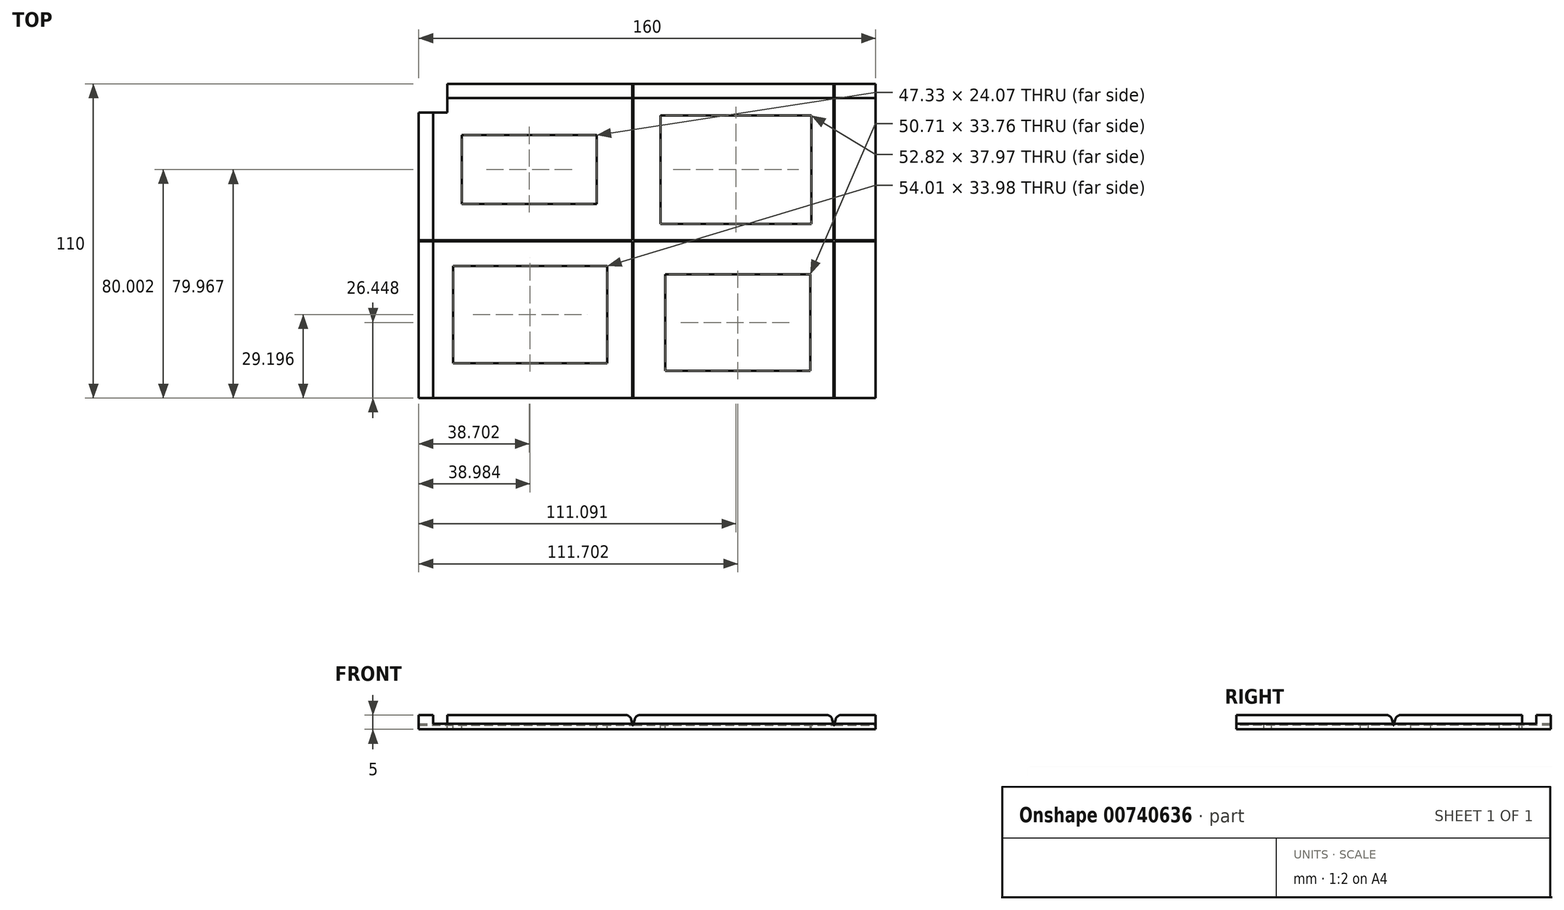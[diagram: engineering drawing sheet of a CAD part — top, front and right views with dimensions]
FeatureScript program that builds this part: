
annotation { "Feature Type Name" : "Feature", "Feature Type Description" : "" }
export const myFeature = defineFeature(function(context is Context, id is Id, definition is map)
    precondition{}
    {
        {
            var Q0;
            Q0=qCreatedBy(makeId("Top.planeOp"),FACE);
            var sketch = newSketch(context, id + "F0", { "sketchPlane" : qUnion([Q0])});
            skLineSegment(sketch, "E0.bottom", {"start": v(-39.4, 71.12) * mm, "end": v(120.6, 71.12) * mm});
            skLineSegment(sketch, "E0.top", {"start": v(-39.4, -38.88) * mm, "end": v(120.6, -38.88) * mm});
            skLineSegment(sketch, "E0.left", {"start": v(-39.4, 71.12) * mm, "end": v(-39.4, -38.88) * mm});
            skLineSegment(sketch, "E0.right", {"start": v(120.6, 71.12) * mm, "end": v(120.6, -38.88) * mm});
            skSolve(sketch);
        }
        {
            var Q0;
            Q0 = qSketchRegion(id + "F0", true);
            extrude(context, id + "F1", {"entities" : qUnion([Q0]), "depth" : 2 * mm, "offsetDistance" : 25 * mm});
        }
        {
            var Q0;
            Q0=makeQuery(id+"F1.opExtrude","CAP_FACE",FACE,{"disambiguationData":[OSD([sQuery(id+"F0.wireOp",EDGE,"E0.bottom"),sQuery(id+"F0.wireOp",EDGE,"E0.top"),sQuery(id+"F0.wireOp",EDGE,"E0.left"),sQuery(id+"F0.wireOp",EDGE,"E0.right")])],"isStart":false});
            var sketch = newSketch(context, id + "F2", { "sketchPlane" : qUnion([Q0])});
            skLineSegment(sketch, "E1.bottom", {"start": v(-39.4, 71.12) * mm, "end": v(-34.4, 71.12) * mm});
            skLineSegment(sketch, "E1.top", {"start": v(-39.4, -38.88) * mm, "end": v(-34.4, -38.88) * mm});
            skLineSegment(sketch, "E1.left", {"start": v(-39.4, 71.12) * mm, "end": v(-39.4, -38.88) * mm});
            skLineSegment(sketch, "E1.right", {"start": v(-34.4, 71.12) * mm, "end": v(-34.4, -38.88) * mm});
            skLineSegment(sketch, "E2.bottom", {"start": v(-34.4, -38.88) * mm, "end": v(-34.4, -38.88) * mm});
            skLineSegment(sketch, "E2.top", {"start": v(-34.4, 71.12) * mm, "end": v(-34.4, 71.12) * mm});
            skLineSegment(sketch, "E2.left", {"start": v(-34.4, -38.88) * mm, "end": v(-34.4, 71.12) * mm});
            skLineSegment(sketch, "E2.right", {"start": v(-34.4, -38.88) * mm, "end": v(-34.4, 71.12) * mm});
            skLineSegment(sketch, "E3.bottom", {"start": v(-34.4, 71.12) * mm, "end": v(120.6, 71.12) * mm});
            skLineSegment(sketch, "E3.top", {"start": v(-34.4, 66.12) * mm, "end": v(120.6, 66.12) * mm});
            skLineSegment(sketch, "E3.left", {"start": v(-34.4, 71.12) * mm, "end": v(-34.4, 66.12) * mm});
            skLineSegment(sketch, "E3.right", {"start": v(120.6, 71.12) * mm, "end": v(120.6, 66.12) * mm});
            skSolve(sketch);
        }
        {
            var Q0;
            Q0 = qSketchRegion(id + "F2", true);
            extrude(context, id + "F3", {"entities" : qUnion([Q0]), "operationType" : NewBodyOperationType.ADD, "depth" : 3 * mm, "offsetDistance" : 25 * mm});
        }
        {
            var Q0;
            Q0=makeQuery(id+"F1.opExtrude","CAP_FACE",FACE,{"disambiguationData":[OSD([sQuery(id+"F0.wireOp",EDGE,"E0.bottom"),sQuery(id+"F0.wireOp",EDGE,"E0.top"),sQuery(id+"F0.wireOp",EDGE,"E0.left"),sQuery(id+"F0.wireOp",EDGE,"E0.right")])],"isStart":false});
            var sketch = newSketch(context, id + "F4", { "sketchPlane" : qUnion([Q0])});
            skLineSegment(sketch, "E4.bottom", {"start": v(35.4, 117.02) * mm, "end": v(35.8, 117.02) * mm});
            skLineSegment(sketch, "E4.top", {"start": v(35.4, -85.4) * mm, "end": v(35.8, -85.4) * mm});
            skLineSegment(sketch, "E4.left", {"start": v(35.4, 117.02) * mm, "end": v(35.4, -85.4) * mm});
            skLineSegment(sketch, "E4.right", {"start": v(35.8, 117.02) * mm, "end": v(35.8, -85.4) * mm});
            skLineSegment(sketch, "E5.bottom", {"start": v(105.8, 121.3) * mm, "end": v(106.2, 121.3) * mm});
            skLineSegment(sketch, "E5.top", {"start": v(105.8, -81.13) * mm, "end": v(106.2, -81.13) * mm});
            skLineSegment(sketch, "E5.left", {"start": v(105.8, 121.3) * mm, "end": v(105.8, -81.13) * mm});
            skLineSegment(sketch, "E5.right", {"start": v(106.2, 121.3) * mm, "end": v(106.2, -81.13) * mm});
            skLineSegment(sketch, "E6.bottom", {"start": v(-56.31, 16.32) * mm, "end": v(149.1, 16.32) * mm});
            skLineSegment(sketch, "E6.top", {"start": v(-56.31, 15.92) * mm, "end": v(149.1, 15.92) * mm});
            skLineSegment(sketch, "E6.left", {"start": v(-56.31, 16.32) * mm, "end": v(-56.31, 15.92) * mm});
            skLineSegment(sketch, "E6.right", {"start": v(149.1, 16.32) * mm, "end": v(149.1, 15.92) * mm});
            skSolve(sketch);
        }
        {
            var Q0;
            Q0 = qSketchRegion(id + "F4", true);
            extrude(context, id + "F5", {"entities" : qUnion([Q0]), "operationType" : NewBodyOperationType.REMOVE, "oppositeDirection" : true, "depth" : 0.6 * mm, "offsetDistance" : 25 * mm});
        }
        {
            var Q0;
            Q0 = qSketchRegion(id + "F4", true);
            extrude(context, id + "F6", {"entities" : qUnion([Q0]), "operationType" : NewBodyOperationType.REMOVE, "depth" : 4 * mm, "offsetDistance" : 25 * mm, "hasDraft" : true, "draftAngle" : 15 * degree});
        }
        {
            var Q0;
            {var subQ0=sQuery(id+"F4.wireOp",EDGE,"E6.bottom");var subQ1=sQuery(id+"F2.wireOp",EDGE,"E2.right");Q0=makeQuery(id+"F6.boolean.opBoolean","INTERSECT",EDGE,{"derivedFrom":[makeQuery(id+"F3.opExtrude","CAP_FACE",FACE,{"disambiguationData":[OSD([sQuery(id+"F2.wireOp",EDGE,"E1.bottom"),sQuery(id+"F2.wireOp",EDGE,"E1.top"),sQuery(id+"F2.wireOp",EDGE,"E1.left"),subQ1,sQuery(id+"F2.wireOp",EDGE,"E3.bottom"),sQuery(id+"F2.wireOp",EDGE,"E3.top"),sQuery(id+"F2.wireOp",EDGE,"E3.right")])],"isStart":false}),makeQuery(id+"F6.opExtrude","SWEPT_FACE",FACE,{"disambiguationData":[OSD([subQ0]),TDD([makeQuery(id+"F4.imprint","IMPRINT",EDGE,{"disambiguationData":[TD([[makeQuery(id+"F4.imprint","INTERSECT",VERTEX,{"derivedFrom":[subQ0,sQuery(id+"F4.wireOp",EDGE,"E6.left")]}),-1.0]])],"derivedFrom":subQ0}),makeQuery(id+"F4.imprint","IMPRINT",EDGE,{"disambiguationData":[TD([[makeQuery(id+"F4.imprint","INTERSECT",VERTEX,{"derivedFrom":[sQuery(id+"F4.wireOp",EDGE,"E4.left"),subQ0]}),1.0]])],"derivedFrom":subQ0})])]})]});}
            var Q1;
            {var subQ0=sQuery(id+"F4.wireOp",EDGE,"E6.top");var subQ1=sQuery(id+"F2.wireOp",EDGE,"E2.right");Q1=makeQuery(id+"F6.boolean.opBoolean","INTERSECT",EDGE,{"derivedFrom":[makeQuery(id+"F3.opExtrude","CAP_FACE",FACE,{"disambiguationData":[OSD([sQuery(id+"F2.wireOp",EDGE,"E1.bottom"),sQuery(id+"F2.wireOp",EDGE,"E1.top"),sQuery(id+"F2.wireOp",EDGE,"E1.left"),subQ1,sQuery(id+"F2.wireOp",EDGE,"E3.bottom"),sQuery(id+"F2.wireOp",EDGE,"E3.top"),sQuery(id+"F2.wireOp",EDGE,"E3.right")])],"isStart":false}),makeQuery(id+"F6.opExtrude","SWEPT_FACE",FACE,{"disambiguationData":[OSD([subQ0]),TDD([makeQuery(id+"F4.imprint","IMPRINT",EDGE,{"disambiguationData":[TD([[makeQuery(id+"F4.imprint","INTERSECT",VERTEX,{"derivedFrom":[subQ0,sQuery(id+"F4.wireOp",EDGE,"E6.left")]}),-1.0]])],"derivedFrom":subQ0}),makeQuery(id+"F4.imprint","IMPRINT",EDGE,{"disambiguationData":[TD([[makeQuery(id+"F4.imprint","INTERSECT",VERTEX,{"derivedFrom":[sQuery(id+"F4.wireOp",EDGE,"E4.left"),subQ0]}),1.0]])],"derivedFrom":subQ0})])]})]});}
            var Q2;
            {var subQ0=sQuery(id+"F4.wireOp",EDGE,"E4.left");var subQ1=sQuery(id+"F2.wireOp",EDGE,"E3.top");Q2=makeQuery(id+"F6.boolean.opBoolean","INTERSECT",EDGE,{"derivedFrom":[makeQuery(id+"F3.opExtrude","CAP_FACE",FACE,{"disambiguationData":[OSD([sQuery(id+"F2.wireOp",EDGE,"E1.bottom"),sQuery(id+"F2.wireOp",EDGE,"E1.top"),sQuery(id+"F2.wireOp",EDGE,"E1.left"),sQuery(id+"F2.wireOp",EDGE,"E2.right"),sQuery(id+"F2.wireOp",EDGE,"E3.bottom"),subQ1,sQuery(id+"F2.wireOp",EDGE,"E3.right")])],"isStart":false}),makeQuery(id+"F6.opExtrude","SWEPT_FACE",FACE,{"disambiguationData":[OSD([subQ0]),TDD([makeQuery(id+"F4.imprint","IMPRINT",EDGE,{"disambiguationData":[TD([[makeQuery(id+"F4.imprint","INTERSECT",VERTEX,{"derivedFrom":[sQuery(id+"F4.wireOp",EDGE,"E4.bottom"),subQ0]}),-1.0]])],"derivedFrom":subQ0}),makeQuery(id+"F4.imprint","IMPRINT",EDGE,{"disambiguationData":[TD([[makeQuery(id+"F4.imprint","INTERSECT",VERTEX,{"derivedFrom":[subQ0,sQuery(id+"F4.wireOp",EDGE,"E6.bottom")]}),1.0]])],"derivedFrom":subQ0})])]})]});}
            var Q3;
            {var subQ0=sQuery(id+"F4.wireOp",EDGE,"E4.right");var subQ1=sQuery(id+"F2.wireOp",EDGE,"E3.top");Q3=makeQuery(id+"F6.boolean.opBoolean","INTERSECT",EDGE,{"derivedFrom":[makeQuery(id+"F3.opExtrude","CAP_FACE",FACE,{"disambiguationData":[OSD([sQuery(id+"F2.wireOp",EDGE,"E1.bottom"),sQuery(id+"F2.wireOp",EDGE,"E1.top"),sQuery(id+"F2.wireOp",EDGE,"E1.left"),sQuery(id+"F2.wireOp",EDGE,"E2.right"),sQuery(id+"F2.wireOp",EDGE,"E3.bottom"),subQ1,sQuery(id+"F2.wireOp",EDGE,"E3.right")])],"isStart":false}),makeQuery(id+"F6.opExtrude","SWEPT_FACE",FACE,{"disambiguationData":[OSD([subQ0]),TDD([makeQuery(id+"F4.imprint","IMPRINT",EDGE,{"disambiguationData":[TD([[makeQuery(id+"F4.imprint","INTERSECT",VERTEX,{"derivedFrom":[sQuery(id+"F4.wireOp",EDGE,"E4.bottom"),subQ0]}),-1.0]])],"derivedFrom":subQ0}),makeQuery(id+"F4.imprint","IMPRINT",EDGE,{"disambiguationData":[TD([[makeQuery(id+"F4.imprint","INTERSECT",VERTEX,{"derivedFrom":[subQ0,sQuery(id+"F4.wireOp",EDGE,"E6.bottom")]}),1.0]])],"derivedFrom":subQ0})])]})]});}
            var Q4;
            {var subQ0=sQuery(id+"F4.wireOp",EDGE,"E5.right");var subQ1=sQuery(id+"F2.wireOp",EDGE,"E3.top");Q4=makeQuery(id+"F6.boolean.opBoolean","INTERSECT",EDGE,{"derivedFrom":[makeQuery(id+"F3.opExtrude","CAP_FACE",FACE,{"disambiguationData":[OSD([sQuery(id+"F2.wireOp",EDGE,"E1.bottom"),sQuery(id+"F2.wireOp",EDGE,"E1.top"),sQuery(id+"F2.wireOp",EDGE,"E1.left"),sQuery(id+"F2.wireOp",EDGE,"E2.right"),sQuery(id+"F2.wireOp",EDGE,"E3.bottom"),subQ1,sQuery(id+"F2.wireOp",EDGE,"E3.right")])],"isStart":false}),makeQuery(id+"F6.opExtrude","SWEPT_FACE",FACE,{"disambiguationData":[OSD([subQ0]),TDD([makeQuery(id+"F4.imprint","IMPRINT",EDGE,{"disambiguationData":[TD([[makeQuery(id+"F4.imprint","INTERSECT",VERTEX,{"derivedFrom":[sQuery(id+"F4.wireOp",EDGE,"E5.bottom"),subQ0]}),-1.0]])],"derivedFrom":subQ0}),makeQuery(id+"F4.imprint","IMPRINT",EDGE,{"disambiguationData":[TD([[makeQuery(id+"F4.imprint","INTERSECT",VERTEX,{"derivedFrom":[subQ0,sQuery(id+"F4.wireOp",EDGE,"E6.bottom")]}),1.0]])],"derivedFrom":subQ0})])]})]});}
            var Q5;
            {var subQ0=sQuery(id+"F4.wireOp",EDGE,"E5.left");var subQ1=sQuery(id+"F2.wireOp",EDGE,"E3.top");Q5=makeQuery(id+"F6.boolean.opBoolean","INTERSECT",EDGE,{"derivedFrom":[makeQuery(id+"F3.opExtrude","CAP_FACE",FACE,{"disambiguationData":[OSD([sQuery(id+"F2.wireOp",EDGE,"E1.bottom"),sQuery(id+"F2.wireOp",EDGE,"E1.top"),sQuery(id+"F2.wireOp",EDGE,"E1.left"),sQuery(id+"F2.wireOp",EDGE,"E2.right"),sQuery(id+"F2.wireOp",EDGE,"E3.bottom"),subQ1,sQuery(id+"F2.wireOp",EDGE,"E3.right")])],"isStart":false}),makeQuery(id+"F6.opExtrude","SWEPT_FACE",FACE,{"disambiguationData":[OSD([subQ0]),TDD([makeQuery(id+"F4.imprint","IMPRINT",EDGE,{"disambiguationData":[TD([[makeQuery(id+"F4.imprint","INTERSECT",VERTEX,{"derivedFrom":[sQuery(id+"F4.wireOp",EDGE,"E5.bottom"),subQ0]}),-1.0]])],"derivedFrom":subQ0}),makeQuery(id+"F4.imprint","IMPRINT",EDGE,{"disambiguationData":[TD([[makeQuery(id+"F4.imprint","INTERSECT",VERTEX,{"derivedFrom":[subQ0,sQuery(id+"F4.wireOp",EDGE,"E6.bottom")]}),1.0]])],"derivedFrom":subQ0})])]})]});}
            fillet(context, id + "F7", {"entities" : qUnion([Q0, Q1, Q2, Q3, Q4, Q5]), "radius" : 2 * mm, "tangentPropagation" : true, "allowEdgeOverflow" : false});
        }
        {
            var Q0;
            {var subQ0=sQuery(id+"F2.wireOp",EDGE,"E1.left");var subQ1=sQuery(id+"F2.wireOp",EDGE,"E3.bottom");var subQ2=sQuery(id+"F2.wireOp",EDGE,"E1.bottom");var subQ3=sQuery(id+"F2.wireOp",EDGE,"E2.right");var subQ4=sQuery(id+"F4.wireOp",EDGE,"E6.bottom");var subQ5=sQuery(id+"F4.wireOp",EDGE,"E4.left");var subQ6=makeQuery(id+"F4.imprint","INTERSECT",VERTEX,{"derivedFrom":[subQ5,subQ4]});var subQ8=sQuery(id+"F2.wireOp",EDGE,"E3.top");Q0=makeQuery(id+"F6.boolean.opBoolean","SPLIT",FACE,{"disambiguationData":[TD([makeQuery(id+"F6.opExtrude","SWEPT_FACE",FACE,{"disambiguationData":[OSD([subQ5]),TDD([makeQuery(id+"F4.imprint","IMPRINT",EDGE,{"disambiguationData":[TD([[makeQuery(id+"F4.imprint","INTERSECT",VERTEX,{"derivedFrom":[sQuery(id+"F4.wireOp",EDGE,"E4.bottom"),subQ5]}),-1.0]])],"derivedFrom":subQ5}),makeQuery(id+"F4.imprint","IMPRINT",EDGE,{"disambiguationData":[TD([[subQ6,1.0]])],"derivedFrom":subQ5})])]})])],"derivedFrom":makeQuery(id+"F3.opExtrude","CAP_FACE",FACE,{"disambiguationData":[OSD([subQ2,sQuery(id+"F2.wireOp",EDGE,"E1.top"),subQ0,subQ3,subQ1,subQ8,sQuery(id+"F2.wireOp",EDGE,"E3.right")])],"isStart":false})});}
            var sketch = newSketch(context, id + "F8", { "sketchPlane" : qUnion([Q0])});
            skLineSegment(sketch, "E7.bottom", {"start": v(-39.4, 71.12) * mm, "end": v(-29.4, 71.12) * mm});
            skLineSegment(sketch, "E7.top", {"start": v(-39.4, 61.12) * mm, "end": v(-29.4, 61.12) * mm});
            skLineSegment(sketch, "E7.left", {"start": v(-39.4, 71.12) * mm, "end": v(-39.4, 61.12) * mm});
            skLineSegment(sketch, "E7.right", {"start": v(-29.4, 71.12) * mm, "end": v(-29.4, 61.12) * mm});
            skPoint(sketch, "E7.middle", {"position": v(-34.4, 66.12) * mm});
            skLineSegment(sketch, "E8.bottom", {"start": v(22.96, 53.15) * mm, "end": v(-24.37, 53.15) * mm});
            skLineSegment(sketch, "E8.top", {"start": v(22.96, 29.09) * mm, "end": v(-24.37, 29.09) * mm});
            skLineSegment(sketch, "E8.left", {"start": v(22.96, 53.15) * mm, "end": v(22.96, 29.09) * mm});
            skLineSegment(sketch, "E8.right", {"start": v(-24.37, 53.15) * mm, "end": v(-24.37, 29.09) * mm});
            skLineSegment(sketch, "E9.bottom", {"start": v(26.58, 7.3) * mm, "end": v(-27.43, 7.3) * mm});
            skLineSegment(sketch, "E9.top", {"start": v(26.58, -26.68) * mm, "end": v(-27.43, -26.68) * mm});
            skLineSegment(sketch, "E9.left", {"start": v(26.58, 7.3) * mm, "end": v(26.58, -26.68) * mm});
            skLineSegment(sketch, "E9.right", {"start": v(-27.43, 7.3) * mm, "end": v(-27.43, -26.68) * mm});
            skLineSegment(sketch, "E10.bottom", {"start": v(98.1, 60.07) * mm, "end": v(45.27, 60.07) * mm});
            skLineSegment(sketch, "E10.top", {"start": v(98.1, 22.1) * mm, "end": v(45.27, 22.1) * mm});
            skLineSegment(sketch, "E10.left", {"start": v(98.1, 60.07) * mm, "end": v(98.1, 22.1) * mm});
            skLineSegment(sketch, "E10.right", {"start": v(45.27, 60.07) * mm, "end": v(45.27, 22.1) * mm});
            skLineSegment(sketch, "E11.bottom", {"start": v(97.65, 4.45) * mm, "end": v(46.94, 4.45) * mm});
            skLineSegment(sketch, "E11.top", {"start": v(97.65, -29.31) * mm, "end": v(46.94, -29.31) * mm});
            skLineSegment(sketch, "E11.left", {"start": v(97.65, 4.45) * mm, "end": v(97.65, -29.31) * mm});
            skLineSegment(sketch, "E11.right", {"start": v(46.94, 4.45) * mm, "end": v(46.94, -29.31) * mm});
            skSolve(sketch);
        }
        {
            var Q0;
            Q0 = qSketchRegion(id + "F8", true);
            extrude(context, id + "F9", {"entities" : qUnion([Q0]), "operationType" : NewBodyOperationType.REMOVE, "oppositeDirection" : true, "depth" : 25 * mm, "offsetDistance" : 25 * mm});
        }
    });
